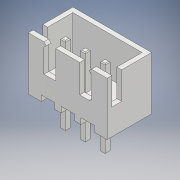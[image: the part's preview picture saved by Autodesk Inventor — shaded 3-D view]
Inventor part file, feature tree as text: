
AUTODESK INVENTOR PART (.ipt)
format: ipt  version: 2017 (Build 210142000, 142)  size: 261,120 bytes
history: native  units: mm
features: other x8, extrude x6, sketch x6, fillet x2, shell x1, chamfer x1, pattern_linear x1, mirror x1, projected_geometry x1
ambient origin geometry x8: Origin, YZ Plane, XZ Plane, XY Plane, X Axis, Y Axis, Z Axis, Center Point
bodies: Solide1 (feature_tree), Solide3 (feature_tree)
feature tree (27):
  other  "Table"
  other  "Connecteur jst 2 broches femelle"
  other  "Connecteur jst 3 broches femelle"
  other  "Connecteur jst 4 broches femelle"
  other  "Connecteur jst 5 broches femelle"
  other  "Connecteur jst 6 broches femelle"
  extrude  "Embase"  TaperAngle=0.0deg  [1 undecoded]
  shell  "Coque1"  Thickness=6.8mm
  other  "Epaississement1"
  extrude  "Rainure"  Depth=0.3mm
  extrude  "Ouverture_avant_2_broches"  Depth=6.8mm TaperAngle=0.0deg
  fillet  "Congé1"  Radius=1.19mm
  other  "Plan de construction3"
  extrude  "Extrusion6"  [1 undecoded]
  extrude  "Extrusion7"  Depth=0.125mm
  chamfer  "Chanfrein2"  Distance=0.75mm
  pattern_linear  "Réseau rectangulaire1"  Spacing1=1.65mm  [1 undecoded]
  extrude  "Ouverture avant sup a2 broches"  Depth=2.85mm
  fillet  "Congé2"  Radius=1.7mm
  mirror  "Symétrie2"
  sketch  "Esquisse1"
  sketch  "Esquisse2"
  sketch  "Esquisse3"
  sketch  "Esquisse6"
  projected_geometry  "Boucle projetée1"
  sketch  "Esquisse7"
  sketch  "Esquisse8"
note: 3 required parameter values undecoded (feature->parameter linkage not recoverable at this tier; creation-order binding heuristic only, values carry confidence <= 0.55)
